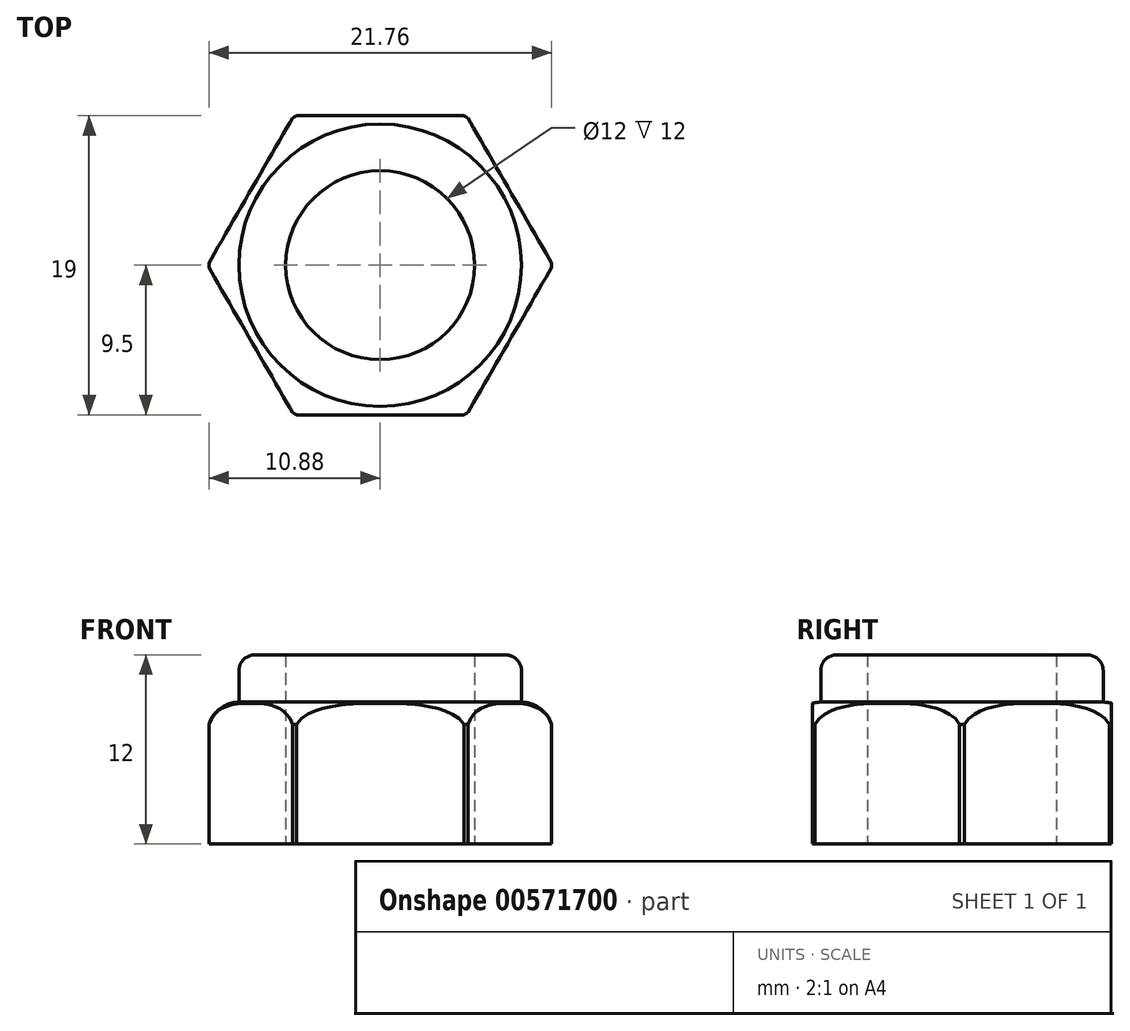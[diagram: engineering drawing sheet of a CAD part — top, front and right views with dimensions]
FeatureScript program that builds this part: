
annotation { "Feature Type Name" : "Feature", "Feature Type Description" : "" }
export const myFeature = defineFeature(function(context is Context, id is Id, definition is map)
    precondition{}
    {
        {
            var Q0;
            Q0=qCreatedBy(makeId("Top.planeOp"),FACE);
            var sketch = newSketch(context, id + "F0", { "sketchPlane" : qUnion([Q0])});
            skCircle(sketch, "E0.cCircle", {"center": v(0, 0) * mm, "radius": 9.5 * mm, "construction": true});
            skLineSegment(sketch, "E0.0", {"start": v(-5.48, 9.5) * mm, "end": v(5.48, 9.5) * mm});
            skLineSegment(sketch, "E0.1", {"start": v(5.48, 9.5) * mm, "end": v(10.97, 0) * mm});
            skLineSegment(sketch, "E0.2", {"start": v(10.97, 0) * mm, "end": v(5.48, -9.5) * mm});
            skLineSegment(sketch, "E0.3", {"start": v(5.48, -9.5) * mm, "end": v(-5.48, -9.5) * mm});
            skLineSegment(sketch, "E0.4", {"start": v(-5.48, -9.5) * mm, "end": v(-10.97, 0) * mm});
            skLineSegment(sketch, "E0.5", {"start": v(-10.97, 0) * mm, "end": v(-5.48, 9.5) * mm});
            skPoint(sketch, "E0.0.midPoint", {"position": v(0, 9.5) * mm});
            skCircle(sketch, "E1", {"center": v(0, 0) * mm, "radius": 6 * mm});
            skSolve(sketch);
        }
        {
            var Q0;
            Q0=makeQuery(id+"F0.imprint","IMPRINT",FACE,{"disambiguationData":[TD([[makeQuery(id+"F0.imprint","IMPRINT",EDGE,{"derivedFrom":sQuery(id+"F0.wireOp",EDGE,"E0.0")}),-1.0]])]});
            extrude(context, id + "F1", {"entities" : qUnion([Q0]), "depth" : 9 * mm, "offsetDistance" : 25 * mm});
        }
        {
            var Q0;
            Q0=qCreatedBy(makeId("Top.planeOp"),FACE);
            var sketch = newSketch(context, id + "F2", { "sketchPlane" : qUnion([Q0])});
            skLineSegment(sketch, "E2", {"start": v(0, 0) * mm, "end": v(5.48, -9.5) * mm});
            skSolve(sketch);
        }
        {
            var Q0;
            Q0=sQuery(id+"F2.wireOp",VERTEX,"E2.end");
            var Q1;
            Q1=makeQuery(id+"F1.opExtrude","CAP_VERTEX",VERTEX,{"disambiguationData":[OSD([sQuery(id+"F0.wireOp",EDGE,"E0.2"),sQuery(id+"F0.wireOp",EDGE,"E0.3")])],"isStart":false});
            var Q2;
            Q2=sQuery(id+"F2.wireOp",VERTEX,"E2.start");
            cPlane(context, id + "F3", {"entities" : qUnion([Q0, Q1, Q2]), "cplaneType" : CPlaneType.THREE_POINT, "offset" : 0 * mm, "width" : 150 * mm, "height" : 150 * mm});
        }
        {
            var Q0;
            Q0=qCreatedBy(id+"F3.planeOp",FACE);
            var sketch = newSketch(context, id + "F4", { "sketchPlane" : qUnion([Q0])});
            skLineSegment(sketch, "E3", {"start": v(0, 0) * mm, "end": v(-10.97, 0) * mm});
            skLineSegment(sketch, "E4", {"start": v(-10.97, 0) * mm, "end": v(-10.97, 7) * mm, "construction": true});
            skLineSegment(sketch, "E5", {"start": v(-8.97, 9) * mm, "end": v(0, 9) * mm});
            skPoint(sketch, "E6.visualSharp", {"position": v(-10.97, 9) * mm});
            skArc(sketch, "E6.filletArc", {"start": v(-8.97, 9) * mm, "mid": v(-10.38, 8.41) * mm, "end": v(-10.97, 7) * mm});
            skLineSegment(sketch, "E7", {"start": v(0, 9) * mm, "end": v(0, 10.47) * mm, "construction": true});
            skLineSegment(sketch, "E8", {"start": v(0, 9) * mm, "end": v(0, 10.47) * mm});
            skLineSegment(sketch, "E9", {"start": v(0, 10.47) * mm, "end": v(-12.8, 10.47) * mm});
            skLineSegment(sketch, "E10", {"start": v(-12.8, 10.47) * mm, "end": v(-12.8, 7.01) * mm});
            skLineSegment(sketch, "E11", {"start": v(-12.8, 7.01) * mm, "end": v(-10.97, 7) * mm});
            skLineSegment(sketch, "E12", {"start": v(0, 0) * mm, "end": v(0, 16.83) * mm});
            skSolve(sketch);
        }
        {
            var Q0;
            Q0=makeQuery(id+"F4.imprint","IMPRINT",FACE,{"disambiguationData":[TD([[makeQuery(id+"F4.imprint","IMPRINT",EDGE,{"derivedFrom":sQuery(id+"F4.wireOp",EDGE,"E5")}),1.0]])]});
            var Q1;
            Q1=sQuery(id+"F4.wireOp",EDGE,"E8");
            revolve(context, id + "F5", {"operationType" : NewBodyOperationType.REMOVE, "entities" : qUnion([Q0]), "axis" : qUnion([Q1]), "revolveType" : RevolveType.FULL, "oppositeDirection" : true});
        }
        {
            var Q0;
            Q0=makeQuery(id+"F1.opExtrude","SWEPT_EDGE",EDGE,{"disambiguationData":[OSD([sQuery(id+"F0.wireOp",EDGE,"E0.4"),sQuery(id+"F0.wireOp",EDGE,"E0.5")])]});
            var Q1;
            Q1=makeQuery(id+"F1.opExtrude","SWEPT_EDGE",EDGE,{"disambiguationData":[OSD([sQuery(id+"F0.wireOp",EDGE,"E0.3"),sQuery(id+"F0.wireOp",EDGE,"E0.4")])]});
            var Q2;
            Q2=makeQuery(id+"F1.opExtrude","SWEPT_EDGE",EDGE,{"disambiguationData":[OSD([sQuery(id+"F0.wireOp",EDGE,"E0.2"),sQuery(id+"F0.wireOp",EDGE,"E0.3")])]});
            var Q3;
            Q3=makeQuery(id+"F1.opExtrude","SWEPT_EDGE",EDGE,{"disambiguationData":[OSD([sQuery(id+"F0.wireOp",EDGE,"E0.0"),sQuery(id+"F0.wireOp",EDGE,"E0.5")])]});
            var Q4;
            Q4=makeQuery(id+"F1.opExtrude","SWEPT_EDGE",EDGE,{"disambiguationData":[OSD([sQuery(id+"F0.wireOp",EDGE,"E0.0"),sQuery(id+"F0.wireOp",EDGE,"E0.1")])]});
            var Q5;
            Q5=makeQuery(id+"F1.opExtrude","SWEPT_EDGE",EDGE,{"disambiguationData":[OSD([sQuery(id+"F0.wireOp",EDGE,"E0.1"),sQuery(id+"F0.wireOp",EDGE,"E0.2")])]});
            chamfer(context, id + "F6", {"entities" : qUnion([Q0, Q1, Q2, Q3, Q4, Q5]), "width" : 0.3 * mm, "tangentPropagation" : true});
        }
        {
            var Q0;
            Q0=makeQuery(id+"F1.opExtrude","CAP_FACE",FACE,{"disambiguationData":[OSD([sQuery(id+"F0.wireOp",EDGE,"E0.0"),sQuery(id+"F0.wireOp",EDGE,"E0.1"),sQuery(id+"F0.wireOp",EDGE,"E0.2"),sQuery(id+"F0.wireOp",EDGE,"E0.3"),sQuery(id+"F0.wireOp",EDGE,"E0.4"),sQuery(id+"F0.wireOp",EDGE,"E0.5"),sQuery(id+"F0.wireOp",EDGE,"E1")])],"isStart":false});
            extrude(context, id + "F7", {"entities" : qUnion([Q0]), "operationType" : NewBodyOperationType.ADD, "depth" : 3 * mm, "offsetDistance" : 25 * mm});
        }
        {
            var Q0;
            Q0=makeQuery(id+"F7.opExtrude","CAP_EDGE",EDGE,{"disambiguationData":[OSD([sQuery(id+"F4.wireOp",EDGE,"E5"),sQuery(id+"F4.wireOp",EDGE,"E6.filletArc")])],"isStart":false});
            fillet(context, id + "F8", {"entities" : qUnion([Q0]), "radius" : 1 * mm, "tangentPropagation" : true, "allowEdgeOverflow" : false});
        }
    });
